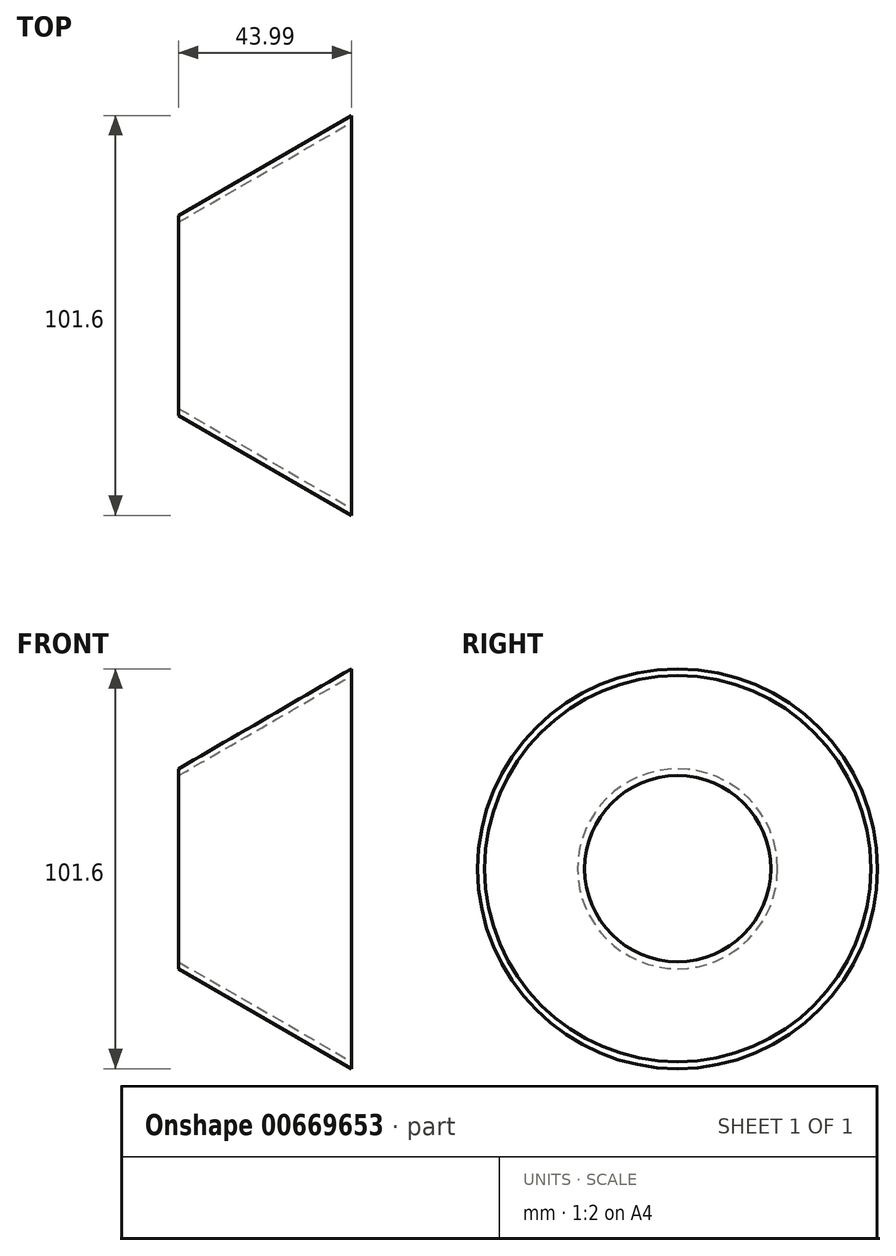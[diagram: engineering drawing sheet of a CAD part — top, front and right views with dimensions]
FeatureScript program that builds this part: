
annotation { "Feature Type Name" : "Feature", "Feature Type Description" : "" }
export const myFeature = defineFeature(function(context is Context, id is Id, definition is map)
    precondition{}
    {
        {
            var Q0;
            Q0=qCreatedBy(makeId("Front.planeOp"),FACE);
            var sketch = newSketch(context, id + "F0", { "sketchPlane" : qUnion([Q0])});
            skLineSegment(sketch, "E0", {"start": v(-59.68, 0) * mm, "end": v(106.48, 0) * mm, "construction": true});
            skLineSegment(sketch, "E1", {"start": v(-44, 0) * mm, "end": v(-44, 25.4) * mm});
            skLineSegment(sketch, "E2", {"start": v(-44, 25.4) * mm, "end": v(0, 50.8) * mm});
            skLineSegment(sketch, "E3", {"start": v(0, 50.8) * mm, "end": v(0, 49.04) * mm});
            skLineSegment(sketch, "E4.0", {"start": v(-44, 23.64) * mm, "end": v(0, 49.04) * mm});
            skLineSegment(sketch, "E5.MirrorCS", {"start": v(-44, 0) * mm, "end": v(-44, -25.4) * mm});
            skLineSegment(sketch, "E6.MirrorCS", {"start": v(-44, -23.64) * mm, "end": v(0, -49.04) * mm});
            skLineSegment(sketch, "E7.MirrorCS", {"start": v(-44, -25.4) * mm, "end": v(0, -50.8) * mm});
            skLineSegment(sketch, "E8.MirrorCS", {"start": v(0, -50.8) * mm, "end": v(0, -49.04) * mm});
            skPoint(sketch, "E9.orphan", {"position": v(0, 0) * mm});
            skSolve(sketch);
        }
        {
            var Q0;
            {var subQ0=sQuery(id+"F0.wireOp",EDGE,"E2");Q0=makeQuery(id+"F0.imprint","IMPRINT",FACE,{"disambiguationData":[TD([[makeQuery(id+"F0.imprint","IMPRINT",EDGE,{"derivedFrom":subQ0}),-1.0]])]});}
            var Q1;
            Q1=sQuery(id+"F0.wireOp",EDGE,"E0");
            revolve(context, id + "F1", {"entities" : qUnion([Q0]), "axis" : qUnion([Q1]), "revolveType" : RevolveType.FULL});
        }
    });
